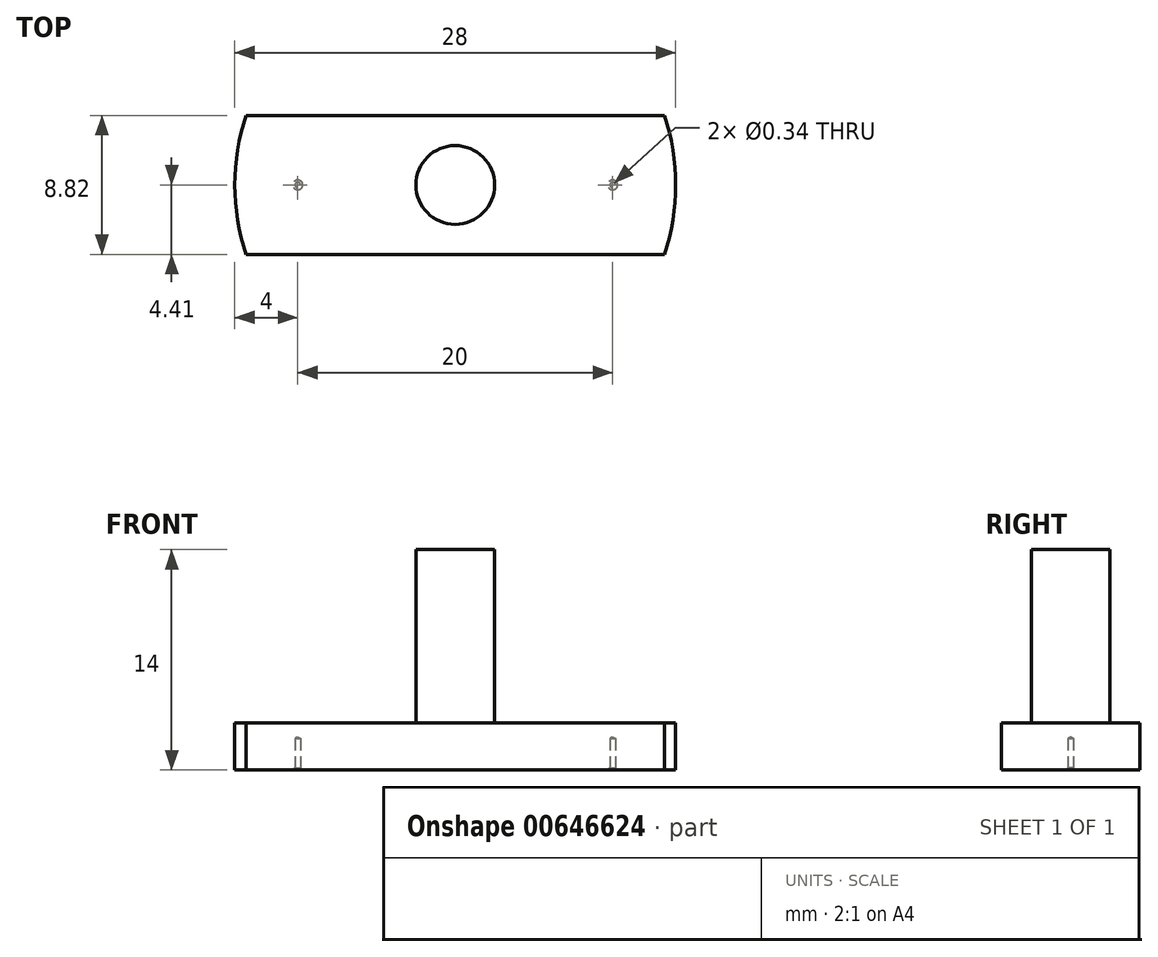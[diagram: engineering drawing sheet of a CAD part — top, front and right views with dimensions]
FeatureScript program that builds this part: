
annotation { "Feature Type Name" : "Feature", "Feature Type Description" : "" }
export const myFeature = defineFeature(function(context is Context, id is Id, definition is map)
    precondition{}
    {
        {
            var Q0;
            Q0=qCreatedBy(makeId("Top.planeOp"),FACE);
            var sketch = newSketch(context, id + "F0", { "sketchPlane" : qUnion([Q0])});
            skArc(sketch, "E0", {"start": v(-13.29, 4.41) * mm, "mid": v(-14, 0) * mm, "end": v(-13.29, -4.41) * mm});
            skLineSegment(sketch, "E1", {"start": v(-13.29, 4.41) * mm, "end": v(13.29, 4.41) * mm});
            skLineSegment(sketch, "E2.MirrorCS", {"start": v(-13.29, -4.41) * mm, "end": v(13.29, -4.41) * mm});
            skArc(sketch, "E3.trimOffspring", {"start": v(13.29, -4.41) * mm, "mid": v(14, 0) * mm, "end": v(13.29, 4.41) * mm});
            skPoint(sketch, "E4", {"position": v(-10, 0) * mm});
            skPoint(sketch, "E5", {"position": v(10, 0) * mm});
            skSolve(sketch);
        }
        {
            var Q0;
            Q0 = qSketchRegion(id + "F0", true);
            extrude(context, id + "F1", {"entities" : qUnion([Q0]), "depth" : 3 * mm, "offsetDistance" : 25 * mm});
        }
        {
            var Q0;
            Q0=sQuery(id+"F0.wireOp",VERTEX,"E4");
            var Q1;
            Q1=sQuery(id+"F0.wireOp",VERTEX,"E5");
            var Q2;
            Q2=makeQuery(id+"F1.opExtrude","SWEPT_BODY",BODY,{"disambiguationData":[OSD([sQuery(id+"F0.wireOp",EDGE,"E0"),sQuery(id+"F0.wireOp",EDGE,"E1"),sQuery(id+"F0.wireOp",EDGE,"E2.MirrorCS"),sQuery(id+"F0.wireOp",EDGE,"E3.trimOffspring")])]});
            hole(context, id + "F2", {"style" : HoleStyle.C_SINK, "endStyle" : HoleEndStyle.BLIND, "oppositeDirection" : true, "holeDiameter" : 0.34 * mm, "cSinkDiameter" : 0.63 * mm, "cSinkAngle" : 90 * degree, "majorDiameter" : 5 * mm, "holeDepth" : 2 * mm, "isTappedThrough" : true, "tappedDepth" : 12 * mm, "tapClearance" : 3, "locations" : qUnion([Q0, Q1]), "scope" : qUnion([Q2])});
        }
        {
            var Q0;
            Q0=makeQuery(id+"F0.imprint","IMPRINT",FACE,{"disambiguationData":[TD([[makeQuery(id+"F0.imprint","IMPRINT",EDGE,{"derivedFrom":sQuery(id+"F0.wireOp",EDGE,"E0")}),1.0]])]});
            var sketch = newSketch(context, id + "F3", { "sketchPlane" : qUnion([Q0])});
            skCircle(sketch, "E6", {"center": v(0, 0) * mm, "radius": 4.25 * mm});
            skSolve(sketch);
        }
        {
            var Q0;
            Q0=sQuery(id+"F3.wireOp",EDGE,"E6");
            extrude(context, id + "F4", {"bodyType" : ToolBodyType.SURFACE, "surfaceEntities" : qUnion([Q0]), "depth" : (16 - 3) * mm, "offsetDistance" : 25 * mm});
        }
        {
            var Q0;
            Q0=qCreatedBy(makeId("Top.planeOp"),FACE);
            var sketch = newSketch(context, id + "F5", { "sketchPlane" : qUnion([Q0])});
            skCircle(sketch, "E7", {"center": v(0, 0) * mm, "radius": 2.5 * mm});
            skSolve(sketch);
        }
        {
            var Q0;
            Q0 = qSketchRegion(id + "F5", true);
            extrude(context, id + "F6", {"entities" : qUnion([Q0]), "operationType" : NewBodyOperationType.ADD, "depth" : (30 - 16) * mm, "offsetDistance" : 25 * mm});
        }
    });
